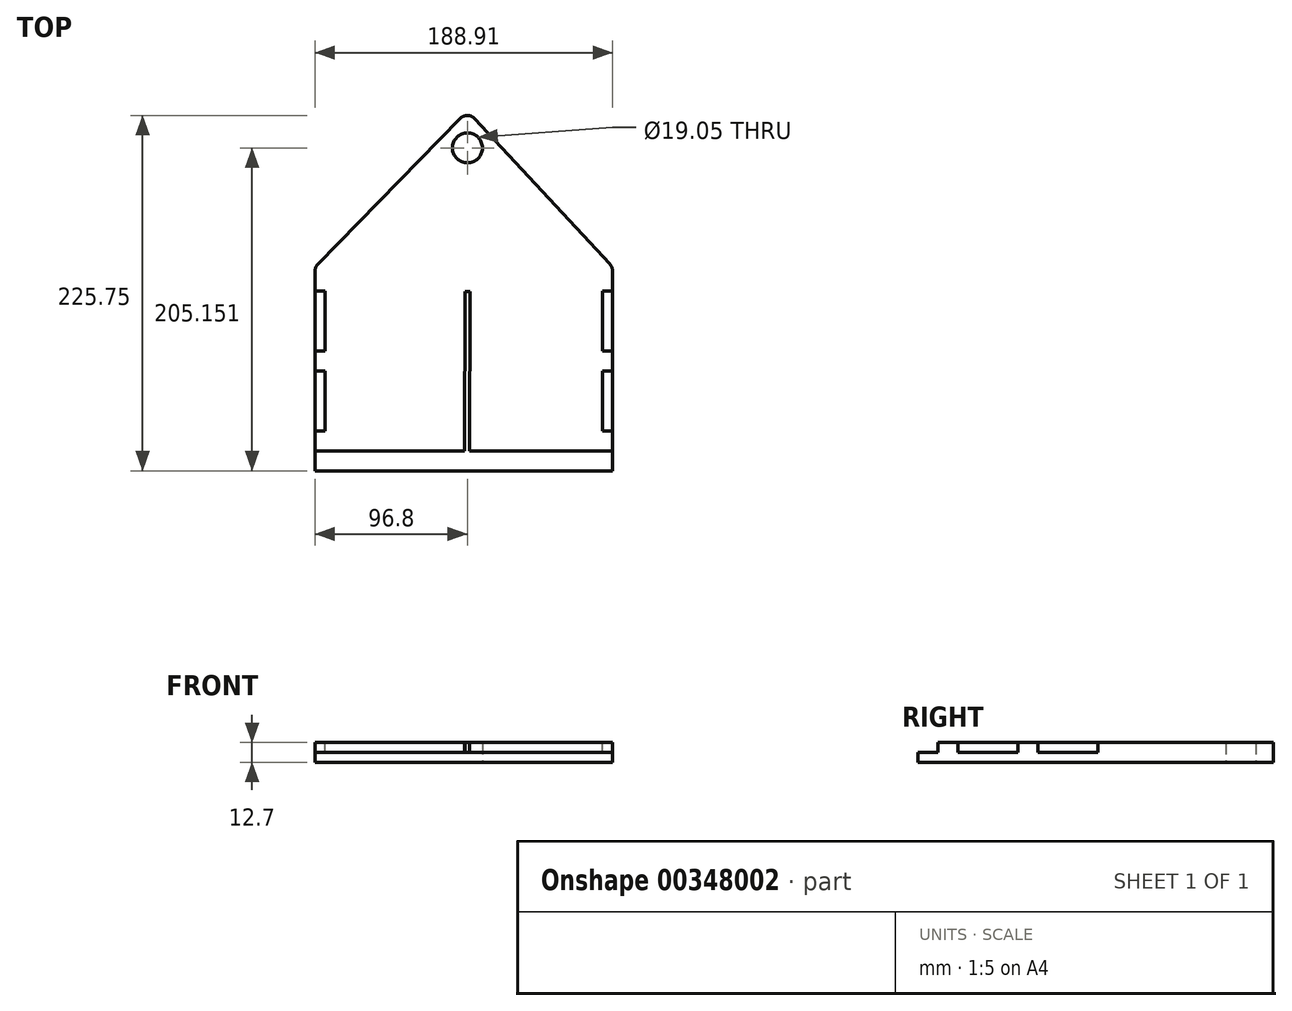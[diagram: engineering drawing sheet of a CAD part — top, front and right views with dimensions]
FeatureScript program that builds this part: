
annotation { "Feature Type Name" : "Feature", "Feature Type Description" : "" }
export const myFeature = defineFeature(function(context is Context, id is Id, definition is map)
    precondition{}
    {
        {
            var Q0;
            Q0=qCreatedBy(makeId("Top.planeOp"),FACE);
            var sketch = newSketch(context, id + "F0", { "sketchPlane" : qUnion([Q0])});
            skLineSegment(sketch, "E0", {"start": v(-96.8, -172.54) * mm, "end": v(92.11, -172.54) * mm});
            skLineSegment(sketch, "E1", {"start": v(92.11, -172.54) * mm, "end": v(92.11, -45.54) * mm});
            skLineSegment(sketch, "E2", {"start": v(90.41, -41.22) * mm, "end": v(4.54, 51.18) * mm});
            skLineSegment(sketch, "E3", {"start": v(-4.66, 51.3) * mm, "end": v(-95, -41.2) * mm});
            skLineSegment(sketch, "E4", {"start": v(-96.8, -45.63) * mm, "end": v(-96.8, -172.54) * mm});
            skPoint(sketch, "E5", {"position": v(-2.35, -172.54) * mm});
            skCircle(sketch, "E6", {"center": v(0, 32.61) * mm, "radius": 9.53 * mm});
            skPoint(sketch, "E7.visualSharp", {"position": v(-96.8, -43.04) * mm});
            skArc(sketch, "E7.filletArc", {"start": v(-95, -41.2) * mm, "mid": v(-96.33, -43.23) * mm, "end": v(-96.8, -45.63) * mm});
            skPoint(sketch, "E8.visualSharp", {"position": v(92.11, -43.04) * mm});
            skArc(sketch, "E8.filletArc", {"start": v(92.11, -45.54) * mm, "mid": v(91.67, -43.22) * mm, "end": v(90.41, -41.22) * mm});
            skPoint(sketch, "E9.visualSharp", {"position": v(0, 56.06) * mm});
            skArc(sketch, "E9.filletArc", {"start": v(4.54, 51.18) * mm, "mid": v(-0.04, 53.2) * mm, "end": v(-4.66, 51.3) * mm});
            skLineSegment(sketch, "E10", {"start": v(0, 67.14) * mm, "end": v(-2.35, -203.13) * mm, "construction": true});
            skSolve(sketch);
        }
        {
            var Q0;
            Q0=makeQuery(id+"F0.imprint","IMPRINT",FACE,{"disambiguationData":[TD([[makeQuery(id+"F0.imprint","IMPRINT",EDGE,{"derivedFrom":sQuery(id+"F0.wireOp",EDGE,"E0")}),1.0]])]});
            extrude(context, id + "F1", {"entities" : qUnion([Q0]), "depth" : 12.7 * mm});
        }
        {
            var Q0;
            Q0=makeQuery(id+"F1.opExtrude","CAP_FACE",FACE,{"disambiguationData":[OSD([sQuery(id+"F0.wireOp",EDGE,"E0"),sQuery(id+"F0.wireOp",EDGE,"E1"),sQuery(id+"F0.wireOp",EDGE,"E2"),sQuery(id+"F0.wireOp",EDGE,"E3"),sQuery(id+"F0.wireOp",EDGE,"E4"),sQuery(id+"F0.wireOp",EDGE,"E6")])],"isStart":false});
            var sketch = newSketch(context, id + "F2", { "sketchPlane" : qUnion([Q0])});
            skLineSegment(sketch, "E11.bottom", {"start": v(-96.8, -58.24) * mm, "end": v(-90.45, -58.24) * mm});
            skLineSegment(sketch, "E11.top", {"start": v(-96.8, -96.34) * mm, "end": v(-90.45, -96.34) * mm});
            skLineSegment(sketch, "E11.left", {"start": v(-96.8, -58.24) * mm, "end": v(-96.8, -96.34) * mm});
            skLineSegment(sketch, "E11.right", {"start": v(-90.45, -58.24) * mm, "end": v(-90.45, -96.34) * mm});
            skLineSegment(sketch, "E12.bottom", {"start": v(-96.8, -109.08) * mm, "end": v(-90.45, -109.08) * mm});
            skLineSegment(sketch, "E12.top", {"start": v(-96.8, -147.18) * mm, "end": v(-90.45, -147.18) * mm});
            skLineSegment(sketch, "E12.left", {"start": v(-96.8, -109.08) * mm, "end": v(-96.8, -147.18) * mm});
            skLineSegment(sketch, "E12.right", {"start": v(-90.45, -109.08) * mm, "end": v(-90.45, -147.18) * mm});
            skLineSegment(sketch, "E13.bottom", {"start": v(92.11, -58.24) * mm, "end": v(85.76, -58.24) * mm});
            skLineSegment(sketch, "E13.top", {"start": v(92.11, -96.34) * mm, "end": v(85.89, -96.34) * mm});
            skLineSegment(sketch, "E13.left", {"start": v(92.11, -58.24) * mm, "end": v(92.11, -96.34) * mm});
            skLineSegment(sketch, "E13.right", {"start": v(85.89, -58.24) * mm, "end": v(85.89, -96.34) * mm});
            skLineSegment(sketch, "E14.bottom", {"start": v(92.11, -109.04) * mm, "end": v(85.89, -109.04) * mm});
            skLineSegment(sketch, "E14.top", {"start": v(92.11, -147.14) * mm, "end": v(85.89, -147.14) * mm});
            skLineSegment(sketch, "E14.left", {"start": v(92.11, -109.04) * mm, "end": v(92.11, -147.14) * mm});
            skLineSegment(sketch, "E14.right", {"start": v(85.89, -109.04) * mm, "end": v(85.89, -147.14) * mm});
            skPoint(sketch, "E15.startSnap0", {"position": v(-0.04, 53.2) * mm});
            skLineSegment(sketch, "E16.bottom", {"start": v(-96.8, -159.84) * mm, "end": v(92.11, -159.84) * mm});
            skLineSegment(sketch, "E16.top", {"start": v(-96.8, -172.54) * mm, "end": v(92.11, -172.54) * mm});
            skLineSegment(sketch, "E16.right", {"start": v(92.11, -159.84) * mm, "end": v(92.11, -172.54) * mm});
            skLineSegment(sketch, "E17.bottom", {"start": v(-1.59, -58.57) * mm, "end": v(1.59, -58.57) * mm});
            skLineSegment(sketch, "E17.left", {"start": v(-1.59, -58.57) * mm, "end": v(-1.73, -159.84) * mm});
            skLineSegment(sketch, "E17.right", {"start": v(1.59, -58.57) * mm, "end": v(1.44, -159.84) * mm});
            skPoint(sketch, "E18", {"position": v(0, -58.57) * mm});
            skLineSegment(sketch, "E19", {"start": v(-96.8, -159.84) * mm, "end": v(-96.8, -172.54) * mm});
            skLineSegment(sketch, "E20", {"start": v(-125.81, -58.15) * mm, "end": v(127.3, -58.15) * mm, "construction": true});
            skSolve(sketch);
        }
        {
            var Q0;
            Q0=makeQuery(id+"F2.imprint","IMPRINT",FACE,{"disambiguationData":[TD([[makeQuery(id+"F2.imprint","IMPRINT",EDGE,{"derivedFrom":sQuery(id+"F2.wireOp",EDGE,"E13.top")}),-1.0]])]});
            var Q1;
            Q1=makeQuery(id+"F2.imprint","IMPRINT",FACE,{"disambiguationData":[TD([[makeQuery(id+"F2.imprint","IMPRINT",EDGE,{"derivedFrom":sQuery(id+"F2.wireOp",EDGE,"E14.bottom")}),1.0]])]});
            var Q2;
            Q2=makeQuery(id+"F2.imprint","IMPRINT",FACE,{"disambiguationData":[TD([[makeQuery(id+"F2.imprint","IMPRINT",EDGE,{"derivedFrom":sQuery(id+"F2.wireOp",EDGE,"E11.bottom")}),-1.0]])]});
            var Q3;
            Q3=makeQuery(id+"F2.imprint","IMPRINT",FACE,{"disambiguationData":[TD([[makeQuery(id+"F2.imprint","IMPRINT",EDGE,{"derivedFrom":sQuery(id+"F2.wireOp",EDGE,"E12.bottom")}),-1.0]])]});
            var Q4;
            Q4=makeQuery(id+"F2.imprint","IMPRINT",FACE,{"disambiguationData":[TD([[makeQuery(id+"F2.imprint","IMPRINT",EDGE,{"derivedFrom":sQuery(id+"F2.wireOp",EDGE,"E16.bottom")}),-1.0]])]});
            var Q5;
            Q5=makeQuery(id+"F2.imprint","IMPRINT",FACE,{"disambiguationData":[TD([[makeQuery(id+"F2.imprint","IMPRINT",EDGE,{"derivedFrom":sQuery(id+"F2.wireOp",EDGE,"E17.bottom")}),-1.0]])]});
            extrude(context, id + "F3", {"entities" : qUnion([Q0, Q1, Q2, Q3, Q4, Q5]), "operationType" : NewBodyOperationType.REMOVE, "oppositeDirection" : true, "depth" : 6.35 * mm});
        }
    });
